# Revit family: 55_CFS498BYC + TCF5534AU
name_source: partatom
category: 衛生器具
units: mm (PartAtom-declared; Revit-internal decimal feet)

## family parameters
OmniClass タイトル = Sanitary, Laundry, and Cleaning Equipment
OmniClass 番号 = 23.45.00.00
パーツ タイプ = 標準
ロード時にボイドで切り取り = はい
丸型コネクタ寸法 = 直径を使用
作業面ベース = いいえ
共有 = いいえ
常に垂直 = はい
部屋計算ポイント = いいえ

## types (1)
- CFS498BYC + HP430-7 + TCF5534AU
    3Dファイル形式 = rfa
    BLCJ仕様バージョン = Version1.0
    URL = https://jp.toto.com
    カウンター色 = <カテゴリ別>
    キーノート = 0表示の場合は商品仕様と設計数量をご確認ください
    データ作成ソフトVer = Revit ver.2019
    パネル色 = <カテゴリ別>
    モデル = CFS498BYC + TCF5534AU
    リモコン距離 = 440  [stored 1.44357 ft]
    リモコン高さ = 850  [stored 2.78871 ft]
    上水負荷単位 = 0
    中水負荷単位 = 0
    付属単位 = TCF5534AU
    企業コード = 504860
    使用水 = 上水
    商品情報URL = https://www.com-et.com
    商品紹介URL = https://jp.toto.com
    奥行 = 664
    幅 = 378
    排気配管 = はい
    排水接続口 = 75/100
    排水接続口情報 = VU,VP75/100塩ビ管
鉛管75/100
    排水芯・排水高さ = 255
    排水配管 = はい
    最低使用圧力 = 0.0 MPa
    最高使用圧力 = 0.0 MPa
    極数 = 2
    構成品番 = CFS498BYC + TCF5534AU
    水配管 = はい
    汚水負荷単位 = 0
    洗浄水量 = 4.8
    流量（L/min） = 0
    消耗品・備品情報 = パッキン：HH11194 給水フィルター付水抜栓：TCM1790 便ふたクッション:TCM6918 便座クッション:高さ3ﾐﾘ：TCM1792R、高さ6ﾐﾘ：TCM8500 脱臭カートリッジ:TCM1788 脱臭フィルター:TCM6827
    消費電力 = 311
    温水配管 = はい
    相 = 1
    給水接続口 = 15A
    給水接続口情報 = R1/2
    給水負荷単位(水栓) = 0
    給水負荷単位(洗浄) = 0
    給湯負荷単位 = 0
    製品リリース年月 = 2021年4月
    製品出荷対象 = 国内
    製造元 = TOTO株式会社
    設置形態 = 床置
    説明 = 掃除口付床置床排水大便器
    負荷分類 = 9_コンセント
    陶器色 = #NW1
    雑排水負荷単位 = 0
    電圧 = 100 V

note: [stored X ft] marks values corroborated as IEEE doubles in the binary element streams (Revit-internal decimal feet)
